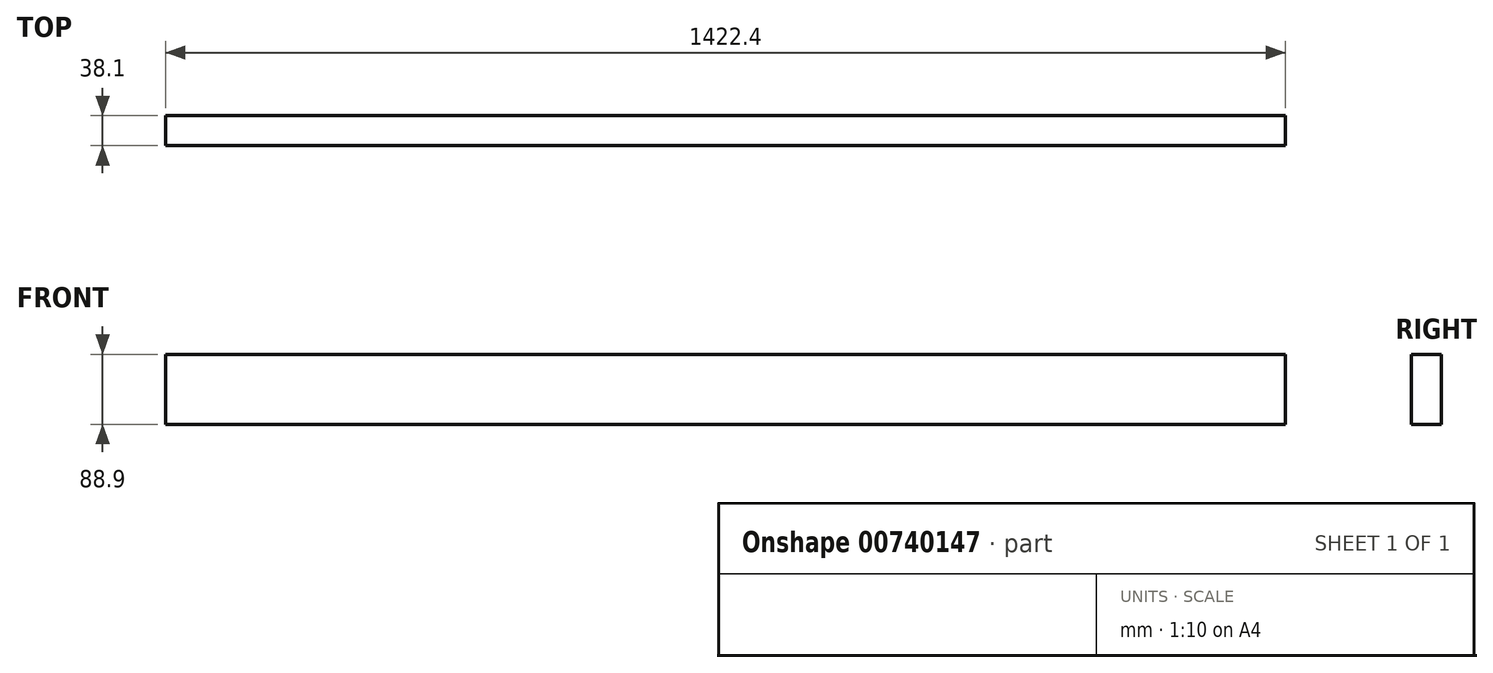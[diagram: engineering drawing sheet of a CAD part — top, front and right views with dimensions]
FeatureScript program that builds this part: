
annotation { "Feature Type Name" : "Feature", "Feature Type Description" : "" }
export const myFeature = defineFeature(function(context is Context, id is Id, definition is map)
    precondition{}
    {
        {
            var Q0;
            Q0=qCreatedBy(makeId("Right.planeOp"),FACE);
            var sketch = newSketch(context, id + "F0", { "sketchPlane" : qUnion([Q0])});
            skLineSegment(sketch, "E0.bottom", {"start": v(-79.68, 85.36) * mm, "end": v(-41.58, 85.36) * mm});
            skLineSegment(sketch, "E0.top", {"start": v(-79.68, -3.54) * mm, "end": v(-41.58, -3.54) * mm});
            skLineSegment(sketch, "E0.left", {"start": v(-79.68, 85.36) * mm, "end": v(-79.68, -3.54) * mm});
            skLineSegment(sketch, "E0.right", {"start": v(-41.58, 85.36) * mm, "end": v(-41.58, -3.54) * mm});
            skSolve(sketch);
        }
        {
            var Q0;
            Q0=makeQuery(id+"F0.imprint","IMPRINT",FACE,{"disambiguationData":[TD([[makeQuery(id+"F0.imprint","IMPRINT",EDGE,{"derivedFrom":sQuery(id+"F0.wireOp",EDGE,"E0.bottom")}),-1.0]])]});
            extrude(context, id + "F1", {"entities" : qUnion([Q0]), "depth" : 1422.4 * mm, "offsetDistance" : 25.4 * mm});
        }
    });
